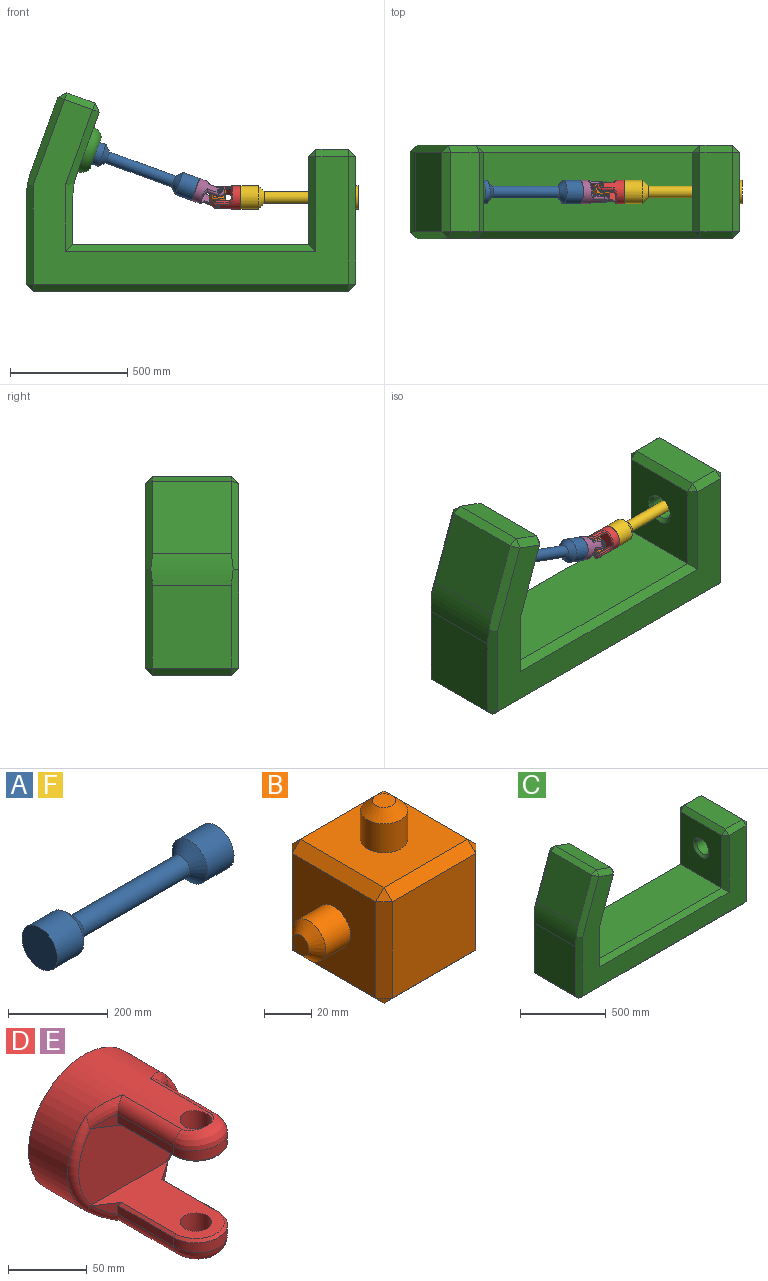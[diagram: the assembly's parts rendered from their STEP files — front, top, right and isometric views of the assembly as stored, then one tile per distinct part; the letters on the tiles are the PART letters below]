
ASSEMBLY  parts=6 mates=6
PART A: 7 faces, bbox 500x100x100 mm
  f0: cylinder r=50mm len=100mm, axis (-1,0,0), area 23561.9mm2, adj f1,f6
  f1: plane 100x100mm, normal (1,0,0), area 7854mm2, adj f0
  f2: cylinder r=25mm len=300mm, axis (-1,0,0), area 47123.9mm2, adj f5,f6
  f3: plane 100x100mm, normal (-1,0,0), area 7854mm2, adj f4
  f4: cylinder r=50mm len=100mm, axis (-1,0,0), area 23561.9mm2, adj f3,f5
  f5: cone r=25mm half-angle=45deg, axis (-1,0,0), area 8330.4mm2, adj f2,f4
  f6: cone r=50mm half-angle=45deg, axis (1,0,0), area 8330.4mm2, adj f0,f2
PART B: 38 faces, bbox 100x60x100 mm
  f0: plane 50x50mm, normal (0,-1,0), area 2500mm2, adj f17,f18,f27,f28
  f1: plane 50x50mm, normal (1,0,0), area 2185.8mm2, adj f12,f19,f28,f29,f33
  f2: plane 50x50mm, normal (0,1,0), area 2500mm2, adj f20,f21,f29,f30
  f3: plane 50x50mm, normal (-1,0,0), area 2185.8mm2, adj f11,f14,f17,f21,f22
  f4: plane 50x50mm, normal (0,0,1), area 2185.8mm2, adj f8,f14,f18,f19,f20
  f5: plane 50x50mm, normal (0,0,-1), area 2185.8mm2, adj f7,f22,f27,f30,f33
  f6: plane 10x10mm, normal (0,0,-1), area 78.5mm2, adj f35
  f7: cylinder r=10mm len=20mm, axis (0,0,-1), area 942.5mm2, adj f5,f35
  f8: cylinder r=10mm len=20mm, axis (0,0,-1), area 942.5mm2, adj f4,f37
  f9: plane 10x10mm, normal (0,0,1), area 78.5mm2, adj f37
  f10: plane 10x10mm, normal (-1,0,0), area 78.5mm2, adj f36
  f11: cylinder r=10mm len=20mm, axis (-1,0,0), area 942.5mm2, adj f3,f36
  f12: cylinder r=10mm len=20mm, axis (-1,0,0), area 942.5mm2, adj f1,f34
  f13: plane 10x10mm, normal (1,0,0), area 78.5mm2, adj f34
  f14: plane 50x5mm, normal (-0.71,0,0.71), area 353.6mm2, adj f3,f4,f15,f16
  f15: plane 5x5mm, normal (-0.58,-0.58,0.58), area 21.7mm2, adj f14,f17,f18
  f16: plane 5x5mm, normal (-0.58,0.58,0.58), area 21.7mm2, adj f14,f20,f21
  f17: plane 50x5mm, normal (-0.71,-0.71,0), area 353.6mm2, adj f0,f3,f15,f23
  f18: plane 50x5mm, normal (0,-0.71,0.71), area 353.6mm2, adj f0,f4,f15,f24
  f19: plane 50x5mm, normal (0.71,0,0.71), area 353.6mm2, adj f1,f4,f24,f25
  f20: plane 50x5mm, normal (0,0.71,0.71), area 353.6mm2, adj f2,f4,f16,f25
  f21: plane 50x5mm, normal (-0.71,0.71,0), area 353.6mm2, adj f2,f3,f16,f26
  f22: plane 50x5mm, normal (-0.71,0,-0.71), area 353.6mm2, adj f3,f5,f23,f26
  f23: plane 5x5mm, normal (-0.58,-0.58,-0.58), area 21.7mm2, adj f17,f22,f27
  f24: plane 5x5mm, normal (0.58,-0.58,0.58), area 21.7mm2, adj f18,f19,f28
  f25: plane 5x5mm, normal (0.58,0.58,0.58), area 21.7mm2, adj f19,f20,f29
  f26: plane 5x5mm, normal (-0.58,0.58,-0.58), area 21.7mm2, adj f21,f22,f30
  f27: plane 50x5mm, normal (0,-0.71,-0.71), area 353.6mm2, adj f0,f5,f23,f31
  f28: plane 50x5mm, normal (0.71,-0.71,0), area 353.6mm2, adj f0,f1,f24,f31
  f29: plane 50x5mm, normal (0.71,0.71,0), area 353.6mm2, adj f1,f2,f25,f32
  f30: plane 50x5mm, normal (0,0.71,-0.71), area 353.6mm2, adj f2,f5,f26,f32
  f31: plane 5x5mm, normal (0.58,-0.58,-0.58), area 21.7mm2, adj f27,f28,f33
  f32: plane 5x5mm, normal (0.58,0.58,-0.58), area 21.7mm2, adj f29,f30,f33
  f33: plane 50x5mm, normal (0.71,0,-0.71), area 353.6mm2, adj f1,f5,f31,f32
  f34: cone r=5mm half-angle=45deg, axis (-1,0,0), area 333.2mm2, adj f12,f13
  f35: cone r=10mm half-angle=45deg, axis (0,0,1), area 333.2mm2, adj f6,f7
  f36: cone r=10mm half-angle=45deg, axis (1,0,0), area 333.2mm2, adj f10,f11
  f37: cone r=5mm half-angle=45deg, axis (0,0,-1), area 333.2mm2, adj f8,f9
PART C: 59 faces, bbox 1408.6x400x847.2 mm
  f0: plane 545.21x340mm, normal (1,0,0), area 172098.9mm2, adj f39,f48,f49,f53,f58
  f1: plane 340x140mm, normal (0,0,1), area 47600mm2, adj f30,f38,f39,f40
  f2: plane 375.21x340mm, normal (-1,0,0), area 114298.9mm2, adj f3,f29,f30,f31,f57
  f3: plane 1008.61x340mm, normal (0,0,1), area 342928.5mm2, adj f2,f4,f24,f25
  f4: plane 340x196.85mm, normal (1,0,0), area 66929.5mm2, adj f3,f20,f21,f55
  f5: plane 340x255.98mm, normal (0.94,0,-0.34), area 61204.5mm2, adj f15,f16,f17,f18,f55
  f6: plane 340x120.22mm, normal (0.34,0,0.94), area 43499.1mm2, adj f18,f23,f26,f27
  f7: plane 340x308.31mm, normal (-0.94,0,0.34), area 111551mm2, adj f27,f33,f36,f54
  f8: plane 354.13x340mm, normal (-1,0,0), area 120402.7mm2, adj f37,f41,f42,f54
  f9: plane 1348.61x340mm, normal (0,0,-1), area 458528.5mm2, adj f42,f47,f50,f53
  f10: plane 1348.61x788.98mm, normal (0,-1,0), area 332010.8mm2, adj f16,f20,f23,f24,f29,f33,f37,f38
  f11: plane 1348.61x788.98mm, normal (0,1,0), area 332010.8mm2, adj f17,f21,f25,f26,f31,f36,f40,f41
  f12: cylinder r=50mm len=104.79mm, axis (-0.94,0,0.34), area 9934.6mm2, adj f13,f56
  f13: plane 100x93.97mm, normal (0.94,0,-0.34), area 7854mm2, adj f12
  f14: cylinder r=50mm len=170mm, axis (1,0,0), area 53407.1mm2, adj f57,f58
  f15: torus R=50mm, axis (0.94,0,-0.34), area 31909mm2, adj f5,f56
  f16: plane 321.44x142.94mm, normal (0.66,-0.71,-0.24), area 14258.5mm2, adj f5,f10,f19,f20,f55
  f17: plane 321.44x142.94mm, normal (0.66,0.71,-0.24), area 14258.5mm2, adj f5,f11,f21,f22,f55
  f18: plane 340x38.45mm, normal (0.91,0,0.42), area 14425mm2, adj f5,f6,f19,f22
  f19: plane 38.45x30mm, normal (0.74,-0.58,0.35), area 779.4mm2, adj f16,f18,f23
  f20: plane 289.95x34.98mm, normal (0.71,-0.71,0), area 11689.1mm2, adj f4,f10,f16,f24,f55
  f21: plane 289.95x34.98mm, normal (0.71,0.71,0), area 11689.1mm2, adj f4,f11,f17,f25,f55
  f22: plane 38.45x30mm, normal (0.74,0.58,0.35), area 779.4mm2, adj f17,f18,f26
  f23: plane 130.48x71.95mm, normal (0.24,-0.71,0.66), area 5428mm2, adj f6,f10,f19,f28
  f24: plane 1068.61x30mm, normal (0,-0.71,0.71), area 44064.6mm2, adj f3,f10,f20,f29
  f25: plane 1068.61x30mm, normal (0,0.71,0.71), area 44064.6mm2, adj f3,f11,f21,f31
  f26: plane 130.48x71.95mm, normal (0.24,0.71,0.66), area 5428mm2, adj f6,f11,f22,f32
  f27: plane 340x38.45mm, normal (-0.42,0,0.91), area 14425mm2, adj f6,f7,f28,f32
  f28: plane 38.45x30mm, normal (-0.35,-0.58,0.74), area 779.4mm2, adj f23,f27,f33
  f29: plane 405.21x30mm, normal (-0.71,-0.71,0), area 16555.3mm2, adj f2,f10,f24,f34
  f30: plane 340x30mm, normal (-0.71,0,0.71), area 14425mm2, adj f1,f2,f34,f35
  f31: plane 405.21x30mm, normal (-0.71,0.71,0), area 16555.3mm2, adj f2,f11,f25,f35
  f32: plane 38.45x30mm, normal (-0.35,0.58,0.74), area 779.4mm2, adj f26,f27,f36
  f33: plane 379.87x158.45mm, normal (-0.66,-0.71,0.24), area 16596.9mm2, adj f7,f10,f28,f37,f54
  f34: plane 30x30mm, normal (-0.58,-0.58,0.58), area 779.4mm2, adj f29,f30,f38
  f35: plane 30x30mm, normal (-0.58,0.58,0.58), area 779.4mm2, adj f30,f31,f40
  f36: plane 379.87x158.45mm, normal (-0.66,0.71,0.24), area 16596.9mm2, adj f7,f11,f32,f41,f54
  f37: plane 423.59x30mm, normal (-0.71,-0.71,0), area 17701.5mm2, adj f8,f10,f33,f43,f54
  f38: plane 140x30mm, normal (0,-0.71,0.71), area 5939.7mm2, adj f1,f10,f34,f44
  f39: plane 340x30mm, normal (0.71,0,0.71), area 14425mm2, adj f0,f1,f44,f45
  f40: plane 140x30mm, normal (0,0.71,0.71), area 5939.7mm2, adj f1,f11,f35,f45
  f41: plane 423.59x30mm, normal (-0.71,0.71,0), area 17701.5mm2, adj f8,f11,f36,f46,f54
  f42: plane 340x30mm, normal (-0.71,0,-0.71), area 14425mm2, adj f8,f9,f43,f46
  f43: plane 30x30mm, normal (-0.58,-0.58,-0.58), area 779.4mm2, adj f37,f42,f47
  f44: plane 30x30mm, normal (0.58,-0.58,0.58), area 779.4mm2, adj f38,f39,f48
  f45: plane 30x30mm, normal (0.58,0.58,0.58), area 779.4mm2, adj f39,f40,f49
  f46: plane 30x30mm, normal (-0.58,0.58,-0.58), area 779.4mm2, adj f41,f42,f50
  f47: plane 1348.61x30mm, normal (0,-0.71,-0.71), area 57216.8mm2, adj f9,f10,f43,f51
  f48: plane 545.21x30mm, normal (0.71,-0.71,0), area 23131.4mm2, adj f0,f10,f44,f51
  f49: plane 545.21x30mm, normal (0.71,0.71,0), area 23131.4mm2, adj f0,f11,f45,f52
  f50: plane 1348.61x30mm, normal (0,0.71,-0.71), area 57216.8mm2, adj f9,f11,f46,f52
  f51: plane 30x30mm, normal (0.58,-0.58,-0.58), area 779.4mm2, adj f47,f48,f53
  f52: plane 30x30mm, normal (0.58,0.58,-0.58), area 779.4mm2, adj f49,f50,f53
  f53: plane 340x30mm, normal (0.71,0,-0.71), area 14425mm2, adj f0,f9,f51,f52
  f54: cylinder r=400mm len=352.15mm, axis (0,1,0), area 48039.2mm2, adj f7,f8,f33,f36,f37,f41
  f55: cylinder r=327.83mm len=340mm, axis (0,-1,0), area 38527.1mm2, adj f4,f5,f16,f17,f20,f21
  f56: cone r=50mm half-angle=57.7deg, axis (0.94,0,-0.34), area 9672.3mm2, adj f12,f15
  f57: cone r=65mm half-angle=45deg, axis (-1,0,0), area 7664mm2, adj f2,f14
  f58: cone r=50mm half-angle=45deg, axis (1,0,0), area 7664mm2, adj f0,f14
PART D: 35 faces, bbox 108.3x120x100 mm
  f0: plane 78.16x70.21mm, normal (0,0,-1), area 2547.5mm2, adj f2,f6,f7,f16,f17,f18,f20,f22
  f1: plane 78.16x70.21mm, normal (0,0,1), area 2547.5mm2, adj f8,f12,f13,f16,f17,f18,f19,f21
  f2: cylinder r=10mm len=20mm, axis (0,0,-1), area 1256.6mm2, adj f0,f14
  f3: plane 50x6.73mm, normal (1,0,0), area 336.5mm2, adj f4,f7,f25,f32
  f4: cylinder r=20mm len=40mm, axis (0,0,-1), area 422.8mm2, adj f3,f5,f24,f33
  f5: plane 50x6.73mm, normal (-1,0,0), area 336.5mm2, adj f4,f6,f23,f34
  f6: plane 15.83x10.56mm, normal (-0.55,-0.83,0), area 88.1mm2, adj f0,f5,f22,f23,f34
  f7: plane 15.83x10.56mm, normal (0.55,-0.83,0), area 88.1mm2, adj f0,f3,f20,f25,f32
  f8: cylinder r=10mm len=20mm, axis (0,0,-1), area 1256.6mm2, adj f1,f14
  f9: plane 50x6.73mm, normal (1,0,0), area 336.5mm2, adj f10,f13,f26,f29
  f10: cylinder r=20mm len=40mm, axis (0,0,-1), area 422.8mm2, adj f9,f11,f27,f30
  f11: plane 50x6.73mm, normal (-1,0,0), area 336.5mm2, adj f10,f12,f28,f31
  f12: plane 15.83x10.56mm, normal (-0.55,-0.83,0), area 88.1mm2, adj f1,f11,f21,f28,f31
  f13: plane 15.83x10.56mm, normal (0.55,-0.83,0), area 88.1mm2, adj f1,f9,f19,f26,f29
  f14: cylinder r=50mm len=110mm, axis (0,1,0), area 14463.6mm2, adj f2,f8,f15,f17,f18,f19,f20,f21
  f15: plane 100x100mm, normal (0,1,0), area 7854mm2, adj f14
  f16: plane 90x60mm, normal (0,-1,0), area 4967.9mm2, adj f0,f1,f17,f18
  f17: torus R=45mm, axis (0,-1,0), area 579.7mm2, adj f0,f1,f14,f16,f21,f22
  f18: torus R=45mm, axis (0,-1,0), area 579.7mm2, adj f0,f1,f14,f16,f19,f20
  f19: bspline ~23.84x19.76mm, area 243.9mm2, adj f1,f13,f14,f18,f26
  f20: bspline ~23.84x19.76mm, area 243.9mm2, adj f0,f7,f14,f18,f25
  f21: bspline ~23.84x19.76mm, area 243.9mm2, adj f1,f12,f14,f17,f28
  f22: bspline ~23.84x19.76mm, area 243.9mm2, adj f0,f6,f14,f17,f23
  f23: cylinder r=10mm len=53.28mm, axis (0,1,0), area 674.6mm2, adj f5,f6,f14,f22,f24
  f24: bspline ~40x22.22mm, area 769.9mm2, adj f4,f14,f23,f25
  f25: cylinder r=10mm len=53.28mm, axis (0,1,0), area 674.6mm2, adj f3,f7,f14,f20,f24
  f26: cylinder r=10mm len=53.28mm, axis (0,1,0), area 674.6mm2, adj f9,f13,f14,f19,f27
  f27: bspline ~40x22.22mm, area 769.9mm2, adj f10,f14,f26,f28
  f28: cylinder r=10mm len=53.28mm, axis (0,1,0), area 674.6mm2, adj f11,f12,f14,f21,f27
  f29: plane 50x2mm, normal (0.71,0,0.71), area 139.5mm2, adj f1,f9,f13,f30
  f30: cone r=18mm half-angle=45deg, axis (0,0,-1), area 168.8mm2, adj f1,f10,f29,f31
  f31: plane 50x2mm, normal (-0.71,0,0.71), area 139.5mm2, adj f1,f11,f12,f30
  f32: plane 50x2mm, normal (0.71,0,-0.71), area 139.5mm2, adj f0,f3,f7,f33
  f33: cone r=20mm half-angle=45deg, axis (0,0,1), area 168.8mm2, adj f0,f4,f32,f34
  f34: plane 50x2mm, normal (-0.71,0,-0.71), area 139.5mm2, adj f0,f5,f6,f33
PART E: same geometry as D
PART F: same geometry as A
PLACE A rot(axis=(-0.98,0.08,0.17),128.9deg) t=(-214.59,0,519.71)mm
PLACE B rot(axis=(-0.24,0.3,0.92),106.7deg) t=(114.28,0.1,399.92)mm
PLACE C t=(-449.51,0,605.21)mm
PLACE D rot(axis=(-0.3,-0.3,-0.91),95.6deg) t=(184.28,0.18,400.03)mm
PLACE E rot(axis=(-0.58,0.69,0.42),157.5deg) t=(48.53,0,423.94)mm
PLACE F rot(axis=(0,-0.31,-0.95),180deg) t=(464.28,0.18,400.03)mm
MATE revolute B.f11 <-> E.f2  axis (-0.21,0.79,-0.58) through (103.75,39.5,370.99)mm
MATE parallel F.f0 <-> C.f0  axis (1,0,0) through (714.28,0.18,400.03)mm
MATE revolute A.f0 <-> C.f15  axis (-0.94,0,0.34) through (-449.51,0,605.21)mm
MATE fastened F.f0 <-> D.f14  axis (-1,0,0) through (214.28,0.18,400.03)mm
MATE revolute B.f7 <-> D.f2  axis (0,-0.59,-0.81) through (114.28,-29.49,359.62)mm
MATE fastened A.f0 <-> E.f14  axis (0.94,0,-0.34) through (20.34,0,434.2)mm
